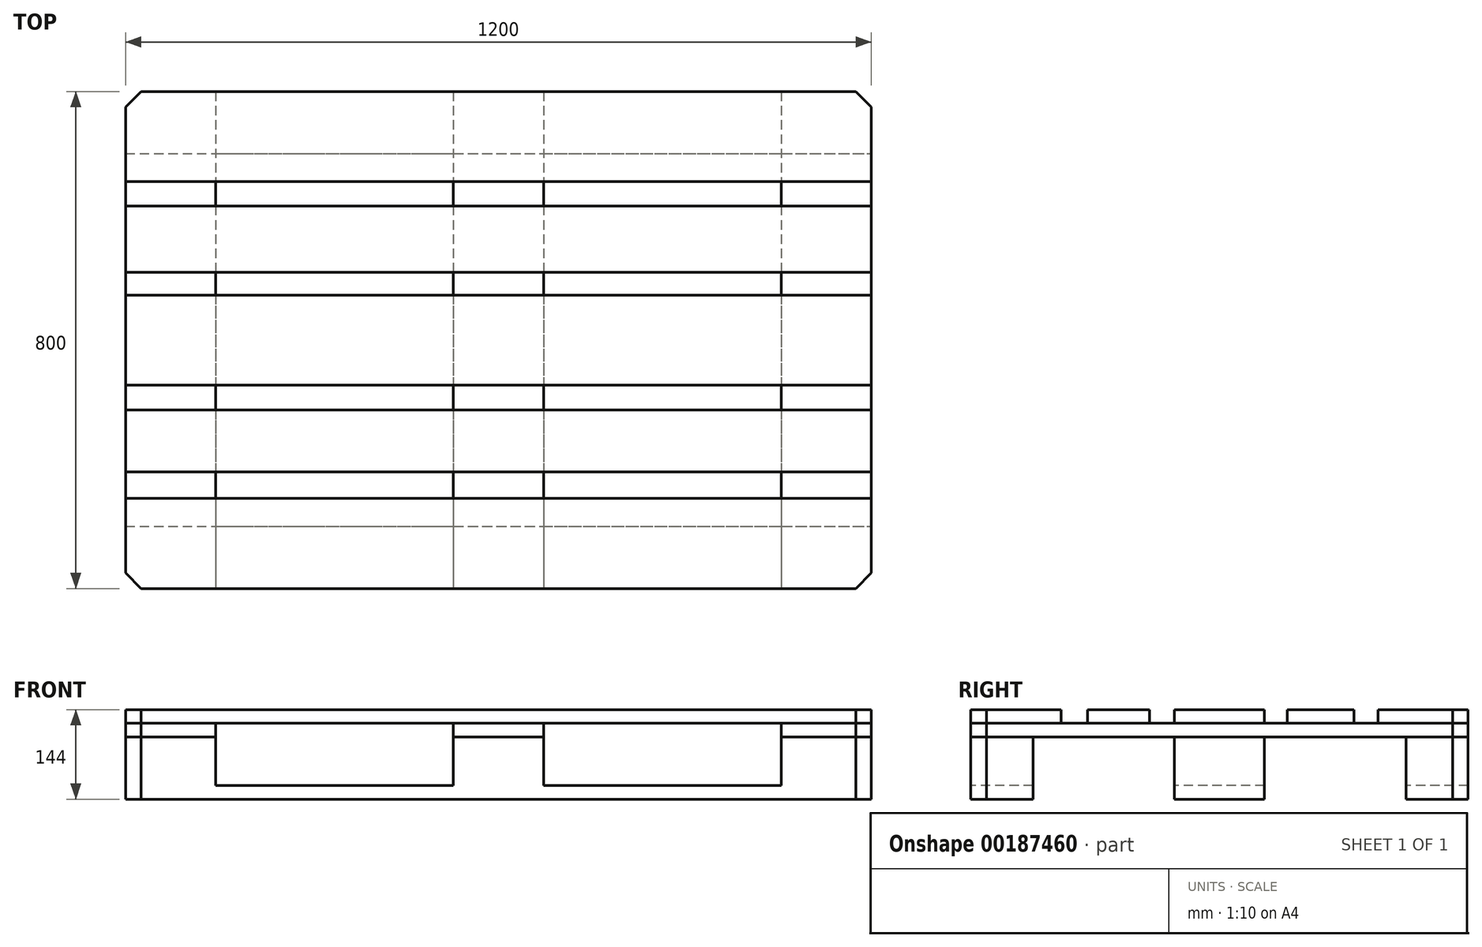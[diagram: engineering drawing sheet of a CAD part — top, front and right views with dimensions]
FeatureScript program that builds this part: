
annotation { "Feature Type Name" : "Feature", "Feature Type Description" : "" }
export const myFeature = defineFeature(function(context is Context, id is Id, definition is map)
    precondition{}
    {
        {
            var Q0;
            Q0=qCreatedBy(makeId("Top.planeOp"),FACE);
            var sketch = newSketch(context, id + "F0", { "sketchPlane" : qUnion([Q0])});
            skLineSegment(sketch, "E0.bottom", {"start": v(600, -400) * mm, "end": v(-600, -400) * mm});
            skLineSegment(sketch, "E0.top", {"start": v(600, 400) * mm, "end": v(-600, 400) * mm});
            skLineSegment(sketch, "E0.left", {"start": v(600, -400) * mm, "end": v(600, 400) * mm});
            skLineSegment(sketch, "E0.right", {"start": v(-600, -400) * mm, "end": v(-600, 400) * mm});
            skPoint(sketch, "E0.middle", {"position": v(0, 0) * mm});
            skLineSegment(sketch, "E1", {"start": v(-600, 300) * mm, "end": v(600, 300) * mm});
            skLineSegment(sketch, "E2", {"start": v(-600, -300) * mm, "end": v(600, -300) * mm});
            skLineSegment(sketch, "E3", {"start": v(-600, 0) * mm, "end": v(600, 0) * mm});
            skLineSegment(sketch, "E4", {"start": v(-600, 72.5) * mm, "end": v(600, 72.5) * mm});
            skLineSegment(sketch, "E5", {"start": v(-600, -72.5) * mm, "end": v(600, -72.5) * mm});
            skSolve(sketch);
        }
        {
            var Q0;
            {var subQ0=sQuery(id+"F0.wireOp",EDGE,"E0.top");Q0=makeQuery(id+"F0.imprint","IMPRINT",FACE,{"disambiguationData":[TD([[makeQuery(id+"F0.imprint","IMPRINT",EDGE,{"derivedFrom":subQ0}),1.0]])]});}
            var Q1;
            {var subQ0=sQuery(id+"F0.wireOp",EDGE,"E3");Q1=makeQuery(id+"F0.imprint","IMPRINT",FACE,{"disambiguationData":[TD([[makeQuery(id+"F0.imprint","IMPRINT",EDGE,{"derivedFrom":subQ0}),1.0]])]});}
            var Q2;
            {var subQ0=sQuery(id+"F0.wireOp",EDGE,"E3");Q2=makeQuery(id+"F0.imprint","IMPRINT",FACE,{"disambiguationData":[TD([[makeQuery(id+"F0.imprint","IMPRINT",EDGE,{"derivedFrom":subQ0}),-1.0]])]});}
            var Q3;
            {var subQ0=sQuery(id+"F0.wireOp",EDGE,"E0.bottom");Q3=makeQuery(id+"F0.imprint","IMPRINT",FACE,{"disambiguationData":[TD([[makeQuery(id+"F0.imprint","IMPRINT",EDGE,{"derivedFrom":subQ0}),-1.0]])]});}
            extrude(context, id + "F1", {"entities" : qUnion([Q0, Q1, Q2, Q3]), "depth" : 22 * mm});
        }
        {
            var Q0;
            Q0=makeQuery(id+"F1.opExtrude","CAP_FACE",FACE,{"disambiguationData":[OSD([sQuery(id+"F0.wireOp",EDGE,"E0.top"),sQuery(id+"F0.wireOp",EDGE,"E0.left"),sQuery(id+"F0.wireOp",EDGE,"E0.right"),sQuery(id+"F0.wireOp",EDGE,"E1")])],"isStart":false});
            var sketch = newSketch(context, id + "F2", { "sketchPlane" : qUnion([Q0])});
            skLineSegment(sketch, "E6", {"start": v(-455, 400) * mm, "end": v(-455, 300) * mm});
            skLineSegment(sketch, "E7", {"start": v(0, 400) * mm, "end": v(0, 300) * mm});
            skLineSegment(sketch, "E8", {"start": v(-72.5, 400) * mm, "end": v(-72.5, 300) * mm});
            skLineSegment(sketch, "E9", {"start": v(72.5, 400) * mm, "end": v(72.5, 300) * mm});
            skLineSegment(sketch, "E10", {"start": v(455, 400) * mm, "end": v(455, 300) * mm});
            skPoint(sketch, "E11.startSnap0", {"position": v(-455, 350) * mm});
            skSolve(sketch);
        }
        {
            var Q0;
            {var subQ0=sQuery(id+"F2.wireOp",EDGE,"E6");Q0=makeQuery(id+"F2.imprint","IMPRINT",FACE,{"disambiguationData":[TD([[makeQuery(id+"F2.imprint","IMPRINT",EDGE,{"derivedFrom":subQ0}),-1.0]])]});}
            var Q1;
            {var subQ0=sQuery(id+"F2.wireOp",EDGE,"E7");Q1=makeQuery(id+"F2.imprint","IMPRINT",FACE,{"disambiguationData":[TD([[makeQuery(id+"F2.imprint","IMPRINT",EDGE,{"derivedFrom":subQ0}),-1.0]])]});}
            var Q2;
            {var subQ0=sQuery(id+"F2.wireOp",EDGE,"E7");Q2=makeQuery(id+"F2.imprint","IMPRINT",FACE,{"disambiguationData":[TD([[makeQuery(id+"F2.imprint","IMPRINT",EDGE,{"derivedFrom":subQ0}),1.0]])]});}
            var Q3;
            {var subQ0=sQuery(id+"F2.wireOp",EDGE,"E10");Q3=makeQuery(id+"F2.imprint","IMPRINT",FACE,{"disambiguationData":[TD([[makeQuery(id+"F2.imprint","IMPRINT",EDGE,{"derivedFrom":subQ0}),1.0]])]});}
            extrude(context, id + "F3", {"entities" : qUnion([Q0, Q1, Q2, Q3]), "operationType" : NewBodyOperationType.ADD, "depth" : 78 * mm});
        }
        {
            var Q0;
            Q0=makeQuery(id+"F1.opExtrude","CAP_FACE",FACE,{"disambiguationData":[OSD([sQuery(id+"F0.wireOp",EDGE,"E0.left"),sQuery(id+"F0.wireOp",EDGE,"E0.right"),sQuery(id+"F0.wireOp",EDGE,"E4"),sQuery(id+"F0.wireOp",EDGE,"E5")])],"isStart":false});
            var sketch = newSketch(context, id + "F4", { "sketchPlane" : qUnion([Q0])});
            skLineSegment(sketch, "E12", {"start": v(-455, 72.5) * mm, "end": v(-455, -72.5) * mm});
            skLineSegment(sketch, "E13", {"start": v(-72.5, 72.5) * mm, "end": v(-72.5, -72.5) * mm});
            skLineSegment(sketch, "E14", {"start": v(72.5, 72.5) * mm, "end": v(72.5, -72.5) * mm});
            skLineSegment(sketch, "E15", {"start": v(455, 72.5) * mm, "end": v(455, -72.5) * mm});
            skSolve(sketch);
        }
        {
            var Q0;
            {var subQ0=sQuery(id+"F4.wireOp",EDGE,"E12");Q0=makeQuery(id+"F4.imprint","IMPRINT",FACE,{"disambiguationData":[TD([[makeQuery(id+"F4.imprint","IMPRINT",EDGE,{"derivedFrom":subQ0}),-1.0]])]});}
            var Q1;
            {var subQ0=sQuery(id+"F4.wireOp",EDGE,"E13");Q1=makeQuery(id+"F4.imprint","IMPRINT",FACE,{"disambiguationData":[TD([[makeQuery(id+"F4.imprint","IMPRINT",EDGE,{"derivedFrom":subQ0}),1.0]])]});}
            var Q2;
            {var subQ0=sQuery(id+"F4.wireOp",EDGE,"E15");Q2=makeQuery(id+"F4.imprint","IMPRINT",FACE,{"disambiguationData":[TD([[makeQuery(id+"F4.imprint","IMPRINT",EDGE,{"derivedFrom":subQ0}),1.0]])]});}
            extrude(context, id + "F5", {"entities" : qUnion([Q0, Q1, Q2]), "operationType" : NewBodyOperationType.ADD, "depth" : 78 * mm});
        }
        {
            var Q0;
            Q0=makeQuery(id+"F1.opExtrude","CAP_FACE",FACE,{"disambiguationData":[OSD([sQuery(id+"F0.wireOp",EDGE,"E0.bottom"),sQuery(id+"F0.wireOp",EDGE,"E0.left"),sQuery(id+"F0.wireOp",EDGE,"E0.right"),sQuery(id+"F0.wireOp",EDGE,"E2")])],"isStart":false});
            var sketch = newSketch(context, id + "F6", { "sketchPlane" : qUnion([Q0])});
            skLineSegment(sketch, "E16", {"start": v(-455, -300) * mm, "end": v(-455, -400) * mm});
            skLineSegment(sketch, "E17", {"start": v(-72.5, -300) * mm, "end": v(-72.5, -400) * mm});
            skLineSegment(sketch, "E18", {"start": v(72.5, -300) * mm, "end": v(72.5, -400) * mm});
            skLineSegment(sketch, "E19", {"start": v(455, -300) * mm, "end": v(455, -400) * mm});
            skSolve(sketch);
        }
        {
            var Q0;
            {var subQ0=sQuery(id+"F6.wireOp",EDGE,"E16");Q0=makeQuery(id+"F6.imprint","IMPRINT",FACE,{"disambiguationData":[TD([[makeQuery(id+"F6.imprint","IMPRINT",EDGE,{"derivedFrom":subQ0}),-1.0]])]});}
            var Q1;
            {var subQ0=sQuery(id+"F6.wireOp",EDGE,"E17");Q1=makeQuery(id+"F6.imprint","IMPRINT",FACE,{"disambiguationData":[TD([[makeQuery(id+"F6.imprint","IMPRINT",EDGE,{"derivedFrom":subQ0}),1.0]])]});}
            var Q2;
            {var subQ0=sQuery(id+"F6.wireOp",EDGE,"E19");Q2=makeQuery(id+"F6.imprint","IMPRINT",FACE,{"disambiguationData":[TD([[makeQuery(id+"F6.imprint","IMPRINT",EDGE,{"derivedFrom":subQ0}),1.0]])]});}
            extrude(context, id + "F7", {"entities" : qUnion([Q0, Q1, Q2]), "operationType" : NewBodyOperationType.ADD, "depth" : 78 * mm});
        }
        {
            var Q0;
            Q0=makeQuery(id+"F3.opExtrude","CAP_FACE",FACE,{"disambiguationData":[OSD([sQuery(id+"F0.wireOp",EDGE,"E0.top"),sQuery(id+"F0.wireOp",EDGE,"E0.right"),sQuery(id+"F0.wireOp",EDGE,"E1"),sQuery(id+"F2.wireOp",EDGE,"E6")])],"isStart":false});
            var sketch = newSketch(context, id + "F8", { "sketchPlane" : qUnion([Q0])});
            skLineSegment(sketch, "E20.bottom", {"start": v(-600, 400) * mm, "end": v(-455, 400) * mm});
            skLineSegment(sketch, "E20.top", {"start": v(-600, -400) * mm, "end": v(-455, -400) * mm});
            skLineSegment(sketch, "E20.left", {"start": v(-600, 400) * mm, "end": v(-600, -400) * mm});
            skLineSegment(sketch, "E20.right", {"start": v(-455, 400) * mm, "end": v(-455, -400) * mm});
            skSolve(sketch);
        }
        {
            var Q0;
            Q0 = qSketchRegion(id + "F8", true);
            extrude(context, id + "F9", {"entities" : qUnion([Q0]), "depth" : 22 * mm});
        }
        {
            var Q0;
            Q0=makeQuery(id+"F3.opExtrude","CAP_FACE",FACE,{"disambiguationData":[OSD([sQuery(id+"F0.wireOp",EDGE,"E0.top"),sQuery(id+"F0.wireOp",EDGE,"E1"),sQuery(id+"F2.wireOp",EDGE,"E8"),sQuery(id+"F2.wireOp",EDGE,"E9")])],"isStart":false});
            var sketch = newSketch(context, id + "F10", { "sketchPlane" : qUnion([Q0])});
            skLineSegment(sketch, "E21.bottom", {"start": v(-72.5, 400) * mm, "end": v(72.5, 400) * mm});
            skLineSegment(sketch, "E21.top", {"start": v(-72.5, -400) * mm, "end": v(72.5, -400) * mm});
            skLineSegment(sketch, "E21.left", {"start": v(-72.5, 400) * mm, "end": v(-72.5, -400) * mm});
            skLineSegment(sketch, "E21.right", {"start": v(72.5, 400) * mm, "end": v(72.5, -400) * mm});
            skSolve(sketch);
        }
        {
            var Q0;
            Q0 = qSketchRegion(id + "F10", true);
            extrude(context, id + "F11", {"entities" : qUnion([Q0]), "depth" : 22 * mm});
        }
        {
            var Q0;
            Q0=makeQuery(id+"F3.opExtrude","CAP_FACE",FACE,{"disambiguationData":[OSD([sQuery(id+"F0.wireOp",EDGE,"E0.top"),sQuery(id+"F0.wireOp",EDGE,"E0.left"),sQuery(id+"F0.wireOp",EDGE,"E1"),sQuery(id+"F2.wireOp",EDGE,"E10")])],"isStart":false});
            var sketch = newSketch(context, id + "F12", { "sketchPlane" : qUnion([Q0])});
            skLineSegment(sketch, "E22.bottom", {"start": v(455, 400) * mm, "end": v(600, 400) * mm});
            skLineSegment(sketch, "E22.top", {"start": v(455, -400) * mm, "end": v(600, -400) * mm});
            skLineSegment(sketch, "E22.left", {"start": v(455, 400) * mm, "end": v(455, -400) * mm});
            skLineSegment(sketch, "E22.right", {"start": v(600, 400) * mm, "end": v(600, -400) * mm});
            skSolve(sketch);
        }
        {
            var Q0;
            Q0 = qSketchRegion(id + "F12", true);
            extrude(context, id + "F13", {"entities" : qUnion([Q0]), "depth" : 22 * mm});
        }
        {
            var Q0;
            Q0=makeQuery(id+"F9.opExtrude","CAP_FACE",FACE,{"disambiguationData":[OSD([sQuery(id+"F8.wireOp",EDGE,"E20.bottom"),sQuery(id+"F8.wireOp",EDGE,"E20.top"),sQuery(id+"F8.wireOp",EDGE,"E20.left"),sQuery(id+"F8.wireOp",EDGE,"E20.right")])],"isStart":false});
            var sketch = newSketch(context, id + "F14", { "sketchPlane" : qUnion([Q0])});
            skLineSegment(sketch, "E23.bottom", {"start": v(-600, 400) * mm, "end": v(600, 400) * mm});
            skLineSegment(sketch, "E23.top", {"start": v(-600, 255) * mm, "end": v(600, 255) * mm});
            skLineSegment(sketch, "E23.left", {"start": v(-600, 400) * mm, "end": v(-600, 255) * mm});
            skLineSegment(sketch, "E23.right", {"start": v(600, 400) * mm, "end": v(600, 255) * mm});
            skSolve(sketch);
        }
        {
            var Q0;
            Q0 = qSketchRegion(id + "F14", true);
            extrude(context, id + "F15", {"entities" : qUnion([Q0]), "depth" : 22 * mm});
        }
        {
            var Q0;
            Q0=makeQuery(id+"F11.opExtrude","CAP_FACE",FACE,{"disambiguationData":[OSD([sQuery(id+"F10.wireOp",EDGE,"E21.bottom"),sQuery(id+"F10.wireOp",EDGE,"E21.top"),sQuery(id+"F10.wireOp",EDGE,"E21.left"),sQuery(id+"F10.wireOp",EDGE,"E21.right")])],"isStart":false});
            var sketch = newSketch(context, id + "F16", { "sketchPlane" : qUnion([Q0])});
            skLineSegment(sketch, "E24.bottom", {"start": v(600, 72.5) * mm, "end": v(-600, 72.5) * mm});
            skLineSegment(sketch, "E24.top", {"start": v(600, -72.5) * mm, "end": v(-600, -72.5) * mm});
            skLineSegment(sketch, "E24.left", {"start": v(600, 72.5) * mm, "end": v(600, -72.5) * mm});
            skLineSegment(sketch, "E24.right", {"start": v(-600, 72.5) * mm, "end": v(-600, -72.5) * mm});
            skPoint(sketch, "E24.middle", {"position": v(0, 0) * mm});
            skSolve(sketch);
        }
        {
            var Q0;
            Q0 = qSketchRegion(id + "F16", true);
            extrude(context, id + "F17", {"entities" : qUnion([Q0]), "depth" : 22 * mm});
        }
        {
            var Q0;
            Q0=makeQuery(id+"F9.opExtrude","CAP_FACE",FACE,{"disambiguationData":[OSD([sQuery(id+"F8.wireOp",EDGE,"E20.bottom"),sQuery(id+"F8.wireOp",EDGE,"E20.top"),sQuery(id+"F8.wireOp",EDGE,"E20.left"),sQuery(id+"F8.wireOp",EDGE,"E20.right")])],"isStart":false});
            var sketch = newSketch(context, id + "F18", { "sketchPlane" : qUnion([Q0])});
            skLineSegment(sketch, "E25.bottom", {"start": v(-600, -400) * mm, "end": v(600, -400) * mm});
            skLineSegment(sketch, "E25.top", {"start": v(-600, -255) * mm, "end": v(600, -255) * mm});
            skLineSegment(sketch, "E25.left", {"start": v(-600, -400) * mm, "end": v(-600, -255) * mm});
            skLineSegment(sketch, "E25.right", {"start": v(600, -400) * mm, "end": v(600, -255) * mm});
            skSolve(sketch);
        }
        {
            var Q0;
            Q0 = qSketchRegion(id + "F18", true);
            extrude(context, id + "F19", {"entities" : qUnion([Q0]), "depth" : 22 * mm});
        }
        {
            var Q0;
            Q0=makeQuery(id+"F9.opExtrude","CAP_FACE",FACE,{"disambiguationData":[OSD([sQuery(id+"F8.wireOp",EDGE,"E20.bottom"),sQuery(id+"F8.wireOp",EDGE,"E20.top"),sQuery(id+"F8.wireOp",EDGE,"E20.left"),sQuery(id+"F8.wireOp",EDGE,"E20.right")])],"isStart":false});
            var sketch = newSketch(context, id + "F20", { "sketchPlane" : qUnion([Q0])});
            skLineSegment(sketch, "E26.bottom", {"start": v(600, 108.92) * mm, "end": v(-600, 108.92) * mm});
            skLineSegment(sketch, "E26.top", {"start": v(600, 216.08) * mm, "end": v(-600, 216.08) * mm});
            skLineSegment(sketch, "E26.left", {"start": v(600, 108.92) * mm, "end": v(600, 216.08) * mm});
            skLineSegment(sketch, "E26.right", {"start": v(-600, 108.92) * mm, "end": v(-600, 216.08) * mm});
            skPoint(sketch, "E26.middle", {"position": v(0, 162.5) * mm});
            skSolve(sketch);
        }
        {
            var Q0;
            Q0 = qSketchRegion(id + "F20", true);
            extrude(context, id + "F21", {"entities" : qUnion([Q0]), "depth" : 22 * mm});
        }
        {
            var Q0;
            Q0=makeQuery(id+"F9.opExtrude","CAP_FACE",FACE,{"disambiguationData":[OSD([sQuery(id+"F8.wireOp",EDGE,"E20.bottom"),sQuery(id+"F8.wireOp",EDGE,"E20.top"),sQuery(id+"F8.wireOp",EDGE,"E20.left"),sQuery(id+"F8.wireOp",EDGE,"E20.right")])],"isStart":false});
            var sketch = newSketch(context, id + "F22", { "sketchPlane" : qUnion([Q0])});
            skLineSegment(sketch, "E27.bottom", {"start": v(600, -112.5) * mm, "end": v(-600, -112.5) * mm});
            skLineSegment(sketch, "E27.top", {"start": v(600, -212.5) * mm, "end": v(-600, -212.5) * mm});
            skLineSegment(sketch, "E27.left", {"start": v(600, -112.5) * mm, "end": v(600, -212.5) * mm});
            skLineSegment(sketch, "E27.right", {"start": v(-600, -112.5) * mm, "end": v(-600, -212.5) * mm});
            skPoint(sketch, "E27.middle", {"position": v(0, -162.5) * mm});
            skSolve(sketch);
        }
        {
            var Q0;
            Q0 = qSketchRegion(id + "F22", true);
            extrude(context, id + "F23", {"entities" : qUnion([Q0]), "depth" : 22 * mm});
        }
        {
            var Q0;
            Q0=makeQuery(id+"F19.opExtrude","SWEPT_EDGE",EDGE,{"disambiguationData":[OSD([sQuery(id+"F18.wireOp",EDGE,"E25.bottom"),sQuery(id+"F18.wireOp",EDGE,"E25.left")])]});
            var Q1;
            Q1=makeQuery(id+"F9.opExtrude","SWEPT_EDGE",EDGE,{"disambiguationData":[OSD([sQuery(id+"F8.wireOp",EDGE,"E20.top"),sQuery(id+"F8.wireOp",EDGE,"E20.left")])]});
            var Q2;
            {var subQ0=sQuery(id+"F0.wireOp",EDGE,"E0.right");var subQ1=sQuery(id+"F0.wireOp",EDGE,"E0.bottom");Q2=makeQuery(id+"F7.boolean.opBoolean","MERGE",EDGE,{"derivedFrom":[makeQuery(id+"F1.opExtrude","SWEPT_EDGE",EDGE,{"disambiguationData":[OSD([subQ1,subQ0])]}),makeQuery(id+"F7.opExtrude","SWEPT_EDGE",EDGE,{"disambiguationData":[OSD([subQ1,subQ0])]})]});}
            var Q3;
            Q3=makeQuery(id+"F19.opExtrude","SWEPT_EDGE",EDGE,{"disambiguationData":[OSD([sQuery(id+"F18.wireOp",EDGE,"E25.bottom"),sQuery(id+"F18.wireOp",EDGE,"E25.right")])]});
            var Q4;
            Q4=makeQuery(id+"F13.opExtrude","SWEPT_EDGE",EDGE,{"disambiguationData":[OSD([sQuery(id+"F12.wireOp",EDGE,"E22.top"),sQuery(id+"F12.wireOp",EDGE,"E22.right")])]});
            var Q5;
            {var subQ0=sQuery(id+"F0.wireOp",EDGE,"E0.left");var subQ1=sQuery(id+"F0.wireOp",EDGE,"E0.bottom");Q5=makeQuery(id+"F7.boolean.opBoolean","MERGE",EDGE,{"derivedFrom":[makeQuery(id+"F1.opExtrude","SWEPT_EDGE",EDGE,{"disambiguationData":[OSD([subQ1,subQ0])]}),makeQuery(id+"F7.opExtrude","SWEPT_EDGE",EDGE,{"disambiguationData":[OSD([subQ1,subQ0])]})]});}
            var Q6;
            Q6=makeQuery(id+"F15.opExtrude","SWEPT_EDGE",EDGE,{"disambiguationData":[OSD([sQuery(id+"F14.wireOp",EDGE,"E23.bottom"),sQuery(id+"F14.wireOp",EDGE,"E23.right")])]});
            var Q7;
            Q7=makeQuery(id+"F13.opExtrude","SWEPT_EDGE",EDGE,{"disambiguationData":[OSD([sQuery(id+"F12.wireOp",EDGE,"E22.bottom"),sQuery(id+"F12.wireOp",EDGE,"E22.right")])]});
            var Q8;
            {var subQ0=sQuery(id+"F0.wireOp",EDGE,"E0.left");var subQ1=sQuery(id+"F0.wireOp",EDGE,"E0.top");Q8=makeQuery(id+"F3.boolean.opBoolean","MERGE",EDGE,{"derivedFrom":[makeQuery(id+"F1.opExtrude","SWEPT_EDGE",EDGE,{"disambiguationData":[OSD([subQ1,subQ0])]}),makeQuery(id+"F3.opExtrude","SWEPT_EDGE",EDGE,{"disambiguationData":[OSD([subQ1,subQ0])]})]});}
            var Q9;
            Q9=makeQuery(id+"F15.opExtrude","SWEPT_EDGE",EDGE,{"disambiguationData":[OSD([sQuery(id+"F14.wireOp",EDGE,"E23.bottom"),sQuery(id+"F14.wireOp",EDGE,"E23.left")])]});
            var Q10;
            Q10=makeQuery(id+"F9.opExtrude","SWEPT_EDGE",EDGE,{"disambiguationData":[OSD([sQuery(id+"F8.wireOp",EDGE,"E20.bottom"),sQuery(id+"F8.wireOp",EDGE,"E20.left")])]});
            var Q11;
            {var subQ0=sQuery(id+"F0.wireOp",EDGE,"E0.right");var subQ1=sQuery(id+"F0.wireOp",EDGE,"E0.top");Q11=makeQuery(id+"F3.boolean.opBoolean","MERGE",EDGE,{"derivedFrom":[makeQuery(id+"F1.opExtrude","SWEPT_EDGE",EDGE,{"disambiguationData":[OSD([subQ1,subQ0])]}),makeQuery(id+"F3.opExtrude","SWEPT_EDGE",EDGE,{"disambiguationData":[OSD([subQ1,subQ0])]})]});}
            chamfer(context, id + "F24", {"entities" : qUnion([Q0, Q1, Q2, Q3, Q4, Q5, Q6, Q7, Q8, Q9, Q10, Q11]), "width" : 25 * mm, "tangentPropagation" : true});
        }
    });
